# Revit family: Power-ModularDevices-GEWISS-90MCB-MTHP250_3P
name_source: partatom
category: Apparecchi elettrici
revit_build: Autodesk Revit MEP 2016 (Build: 20150220_1215(x64)
units: mm (PartAtom-declared; Revit-internal decimal feet)

## family parameters
Condiviso = Sì
Host = Superficie
Mantenere orientamento annotazione = Sì
Numero OmniClass = 23.80.50.00
Punto di calcolo locali = Sì
Quota connettore circolare = Usa diametro
Taglio con vuoti quando caricato = No
Tipo di parte = Normale
Titolo OmniClass = Terminals for Power Supply

## types (6) — shared parameters
Breaking capacity (EN 60898) = 0.75 x Icn
Breaking capacity EN 60898 (Ics) = 0.75 x Icn
Breaking capacity EN 60898 230V (Icn) = 25000A
Breaking capacity EN 60898 400V (Icn) = 25000A
Breaking capacity EN 60947-2 (Ics) = 75% Icu
Breaking capacity EN 60947-2 230V (Icu) = 30KA
Breaking capacity EN 60947-2 400V (Icu) = 25KA
Catalogue = POWER
Catalogue Range = 90 MCB
Curve = C
Description = HIGH PERFORMANCE MINIATURE CIRCUIT BREAKER
Distanza dal piano = 3 mm  [stored 0.00984252 ft]
Electrical endurance = 10000
Electrocod = 1411
IDF = a5bb6751-9f93-4ffb-a896-71562a4a5b63
IDT = c60f315d-c6fa-4cd9-a51d-3fcd06983766
Immagine tipo = GW93236.jpg
Insulation voltage = 500V
Label = MTHP 250
Maximum operating voltage = 440V AC / 220V DC
Mechanical endurance = 20.000
Minimum operating voltage = 12V ac/dc
No. Chorus modules = 4,5
No. modules = 4.5
No. of modules EN 50022 = 4,5
No. of poles = 3P
Number of poles = 3P
Numero di poli_ = 1
Operating temperature = -25 +60 °C
Produttore = GEWISS S.p.A.
Prospetto di default = 1219 mm
Rated frequency (Hz) = 50/60 Hz
Rated impulse withstand voltage = 6KV
Rated insulation voltage (Ui) = 500V
Rated tightening torque = 3.5 / 3 (terminals)
Rated voltage = 230-400V
SEO = MCB
Section flexible cable = <=1x50(2) - <=2x25 - <=3x16 mm²
Section rigid cable = <=1x70 - <=2x25 - <=2x25+1x10 mm²
Spostamento_x = -4000 mm  [stored -13.1234 ft]
Standard = EN60898, EN60947-2
Standard; = EN 60898, EN 60947-2
Stocking temperature = -40 +70 °C
Technical sheet = https://www.gewiss.com
URL = https://www.gewiss.com
Version file RFA = 19.0
carico = Altro
potenza in watt = 0 V

## per-type parameters (varying)
| type | Descrizione | EAN code | Modello | Rated current (In) | Rated current: |
| GW93234 - HIGH PERF. MCB 3P C40 25KA 4.5M | HIGH PERF. MCB 3P C40 25KA 4.5M | 8011564115712 | GW93234 | 40A | 40A |
| GW93232 - HIGH PERF. MCB 3P C25 25KA 4.5M | HIGH PERF. MCB 3P C25 25KA 4.5M | 8011564115699 | GW93232 | 25A | 25A |
| GW93236 - HIGH PERF. MCB 3P C63 25KA 4.5M | HIGH PERF. MCB 3P C63 25KA 4.5M | 8011564115736 | GW93236 | 63A | 63A |
| GW93233 - HIGH PERF. MCB 3P C32 25KA 4.5M | HIGH PERF. MCB 3P C32 25KA 4.5M | 8011564115705 | GW93233 | 32A | 32A |
| GW93235 - HIGH PERF. MCB 3P C50 25KA 4.5M | HIGH PERF. MCB 3P C50 25KA 4.5M | 8011564115729 | GW93235 | 50A | 50A |
| GW93231 - HIGH PERF. MCB 3P C20 25KA 4.5M | HIGH PERF. MCB 3P C20 25KA 4.5M | 8011564115682 | GW93231 | 20A | 20A |

note: [stored X ft] marks values corroborated as IEEE doubles in the binary element streams (Revit-internal decimal feet)
